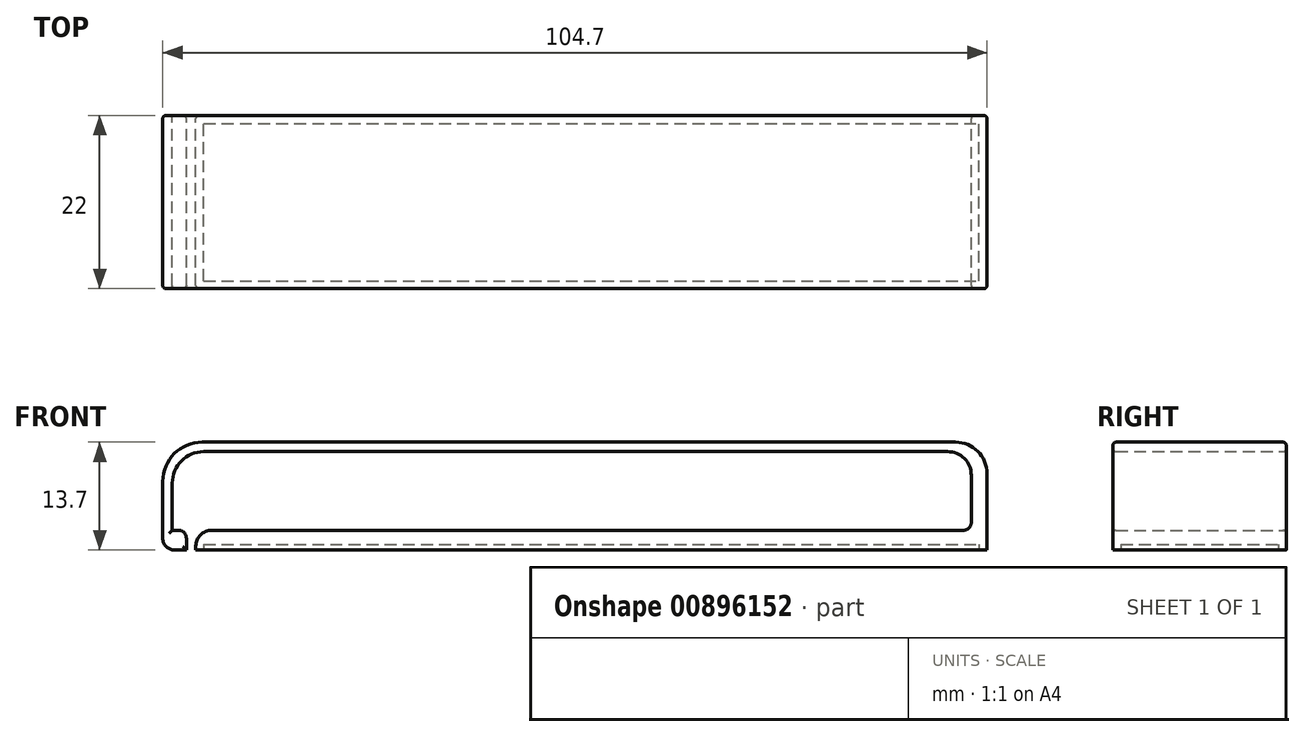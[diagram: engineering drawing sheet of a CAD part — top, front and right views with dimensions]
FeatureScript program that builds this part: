
annotation { "Feature Type Name" : "Feature", "Feature Type Description" : "" }
export const myFeature = defineFeature(function(context is Context, id is Id, definition is map)
    precondition{}
    {
        {
            var Q0;
            Q0=qCreatedBy(makeId("Front.planeOp"),FACE);
            var sketch = newSketch(context, id + "F0", { "sketchPlane" : qUnion([Q0])});
            skLineSegment(sketch, "E0.bottom", {"start": v(-79.1, 10.9) * mm, "end": v(16.4, 10.9) * mm});
            skLineSegment(sketch, "E0.top", {"start": v(-81.1, 8.4) * mm, "end": v(19.4, 8.4) * mm});
            skLineSegment(sketch, "E0.left", {"start": v(-81.1, 8.9) * mm, "end": v(-81.1, 8.4) * mm});
            skLineSegment(sketch, "E1.left", {"start": v(19.4, 8.4) * mm, "end": v(19.4, 18.1) * mm});
            skLineSegment(sketch, "E1.right", {"start": v(17.4, 11.9) * mm, "end": v(17.4, 17.9) * mm});
            skLineSegment(sketch, "E2.bottom", {"start": v(14.4, 20.9) * mm, "end": v(-80.1, 20.9) * mm});
            skLineSegment(sketch, "E2.top", {"start": v(15.4, 22.1) * mm, "end": v(-80.3, 22.1) * mm});
            skLineSegment(sketch, "E3.left", {"start": v(-85.3, 17.1) * mm, "end": v(-85.3, 10.9) * mm});
            skLineSegment(sketch, "E3.right", {"start": v(-84.1, 16.9) * mm, "end": v(-84.1, 10.9) * mm});
            skLineSegment(sketch, "E4.bottom", {"start": v(-84.1, 10.9) * mm, "end": v(-83.3, 10.9) * mm});
            skLineSegment(sketch, "E4.top", {"start": v(-83.8, 8.4) * mm, "end": v(-82.3, 8.4) * mm});
            skLineSegment(sketch, "E4.left", {"start": v(-85.3, 10.9) * mm, "end": v(-85.3, 9.9) * mm});
            skLineSegment(sketch, "E4.right", {"start": v(-82.3, 9.9) * mm, "end": v(-82.3, 8.4) * mm});
            skPoint(sketch, "E5.visualSharp", {"position": v(-84.1, 20.9) * mm});
            skArc(sketch, "E5.filletArc", {"start": v(-80.1, 20.9) * mm, "mid": v(-82.92, 19.73) * mm, "end": v(-84.1, 16.9) * mm});
            skPoint(sketch, "E6.visualSharp", {"position": v(-85.3, 22.1) * mm});
            skArc(sketch, "E6.filletArc", {"start": v(-80.3, 22.1) * mm, "mid": v(-83.83, 20.64) * mm, "end": v(-85.3, 17.1) * mm});
            skPoint(sketch, "E7.visualSharp", {"position": v(-82.3, 10.9) * mm});
            skArc(sketch, "E7.filletArc", {"start": v(-82.3, 9.9) * mm, "mid": v(-82.59, 10.6) * mm, "end": v(-83.3, 10.9) * mm});
            skPoint(sketch, "E8.visualSharp", {"position": v(-81.1, 10.9) * mm});
            skArc(sketch, "E8.filletArc", {"start": v(-79.1, 10.9) * mm, "mid": v(-80.5, 10.32) * mm, "end": v(-81.1, 8.9) * mm});
            skPoint(sketch, "E9.visualSharp", {"position": v(17.4, 10.9) * mm});
            skArc(sketch, "E9.filletArc", {"start": v(16.4, 10.9) * mm, "mid": v(17.11, 11.2) * mm, "end": v(17.4, 11.9) * mm});
            skPoint(sketch, "E10.visualSharp", {"position": v(17.4, 20.9) * mm});
            skArc(sketch, "E10.filletArc", {"start": v(17.4, 17.9) * mm, "mid": v(16.53, 20.02) * mm, "end": v(14.4, 20.9) * mm});
            skPoint(sketch, "E11.visualSharp", {"position": v(19.4, 22.1) * mm});
            skArc(sketch, "E11.filletArc", {"start": v(19.4, 18.1) * mm, "mid": v(18.24, 20.93) * mm, "end": v(15.4, 22.1) * mm});
            skPoint(sketch, "E12.visualSharp", {"position": v(-85.3, 8.4) * mm});
            skArc(sketch, "E12.filletArc", {"start": v(-85.3, 9.9) * mm, "mid": v(-84.85, 8.84) * mm, "end": v(-83.8, 8.4) * mm});
            skSolve(sketch);
        }
        {
            var Q0;
            Q0=makeQuery(id+"F0.imprint","IMPRINT",FACE,{"disambiguationData":[TD([[makeQuery(id+"F0.imprint","IMPRINT",EDGE,{"derivedFrom":sQuery(id+"F0.wireOp",EDGE,"E0.bottom")}),-1.0]])]});
            extrude(context, id + "F1", {"entities" : qUnion([Q0]), "depth" : 22 * mm, "offsetDistance" : 25 * mm});
        }
        {
            var Q0;
            Q0=makeQuery(id+"F1.opExtrude","SWEPT_FACE",FACE,{"disambiguationData":[OSD([sQuery(id+"F0.wireOp",EDGE,"E0.top")])]});
            var sketch = newSketch(context, id + "F2", { "sketchPlane" : qUnion([Q0])});
            skLineSegment(sketch, "E13.bottom", {"start": v(-80.1, 21) * mm, "end": v(18.4, 21) * mm});
            skLineSegment(sketch, "E13.top", {"start": v(-80.1, 1) * mm, "end": v(18.4, 1) * mm});
            skLineSegment(sketch, "E13.left", {"start": v(-80.1, 21) * mm, "end": v(-80.1, 1) * mm});
            skLineSegment(sketch, "E13.right", {"start": v(18.4, 21) * mm, "end": v(18.4, 1) * mm});
            skSolve(sketch);
        }
        {
            var Q0;
            Q0=makeQuery(id+"F2.imprint","IMPRINT",FACE,{"disambiguationData":[TD([[makeQuery(id+"F2.imprint","IMPRINT",EDGE,{"derivedFrom":sQuery(id+"F2.wireOp",EDGE,"E13.bottom")}),-1.0]])]});
            extrude(context, id + "F3", {"entities" : qUnion([Q0]), "operationType" : NewBodyOperationType.REMOVE, "flatOperationType" : FlatOperationType.REMOVE, "oppositeDirection" : true, "depth" : 0.7 * mm, "offsetDistance" : 25 * mm, "domain" : OperationDomain.MODEL});
        }
        {
            var Q0;
            Q0=makeQuery(id+"F1.opExtrude","CAP_EDGE",EDGE,{"disambiguationData":[OSD([sQuery(id+"F0.wireOp",EDGE,"E2.top")])],"isStart":false});
            var Q1;
            Q1=makeQuery(id+"F1.opExtrude","CAP_EDGE",EDGE,{"disambiguationData":[OSD([sQuery(id+"F0.wireOp",EDGE,"E2.bottom")])],"isStart":false});
            var Q2;
            Q2=makeQuery(id+"F1.opExtrude","CAP_EDGE",EDGE,{"disambiguationData":[OSD([sQuery(id+"F0.wireOp",EDGE,"E7.filletArc")])],"isStart":false});
            var Q3;
            Q3=makeQuery(id+"F1.opExtrude","CAP_EDGE",EDGE,{"disambiguationData":[OSD([sQuery(id+"F0.wireOp",EDGE,"E4.right")])],"isStart":false});
            var Q4;
            Q4=makeQuery(id+"F1.opExtrude","CAP_EDGE",EDGE,{"disambiguationData":[OSD([sQuery(id+"F0.wireOp",EDGE,"E2.bottom")])],"isStart":true});
            var Q5;
            Q5=makeQuery(id+"F1.opExtrude","CAP_EDGE",EDGE,{"disambiguationData":[OSD([sQuery(id+"F0.wireOp",EDGE,"E2.top")])],"isStart":true});
            var Q6;
            Q6=makeQuery(id+"F1.opExtrude","CAP_EDGE",EDGE,{"disambiguationData":[OSD([sQuery(id+"F0.wireOp",EDGE,"E7.filletArc")])],"isStart":true});
            fillet(context, id + "F4", {"entities" : qUnion([Q0, Q1, Q2, Q3, Q4, Q5, Q6]), "radius" : 0.4 * mm, "tangentPropagation" : true, "allowEdgeOverflow" : false});
        }
    });
